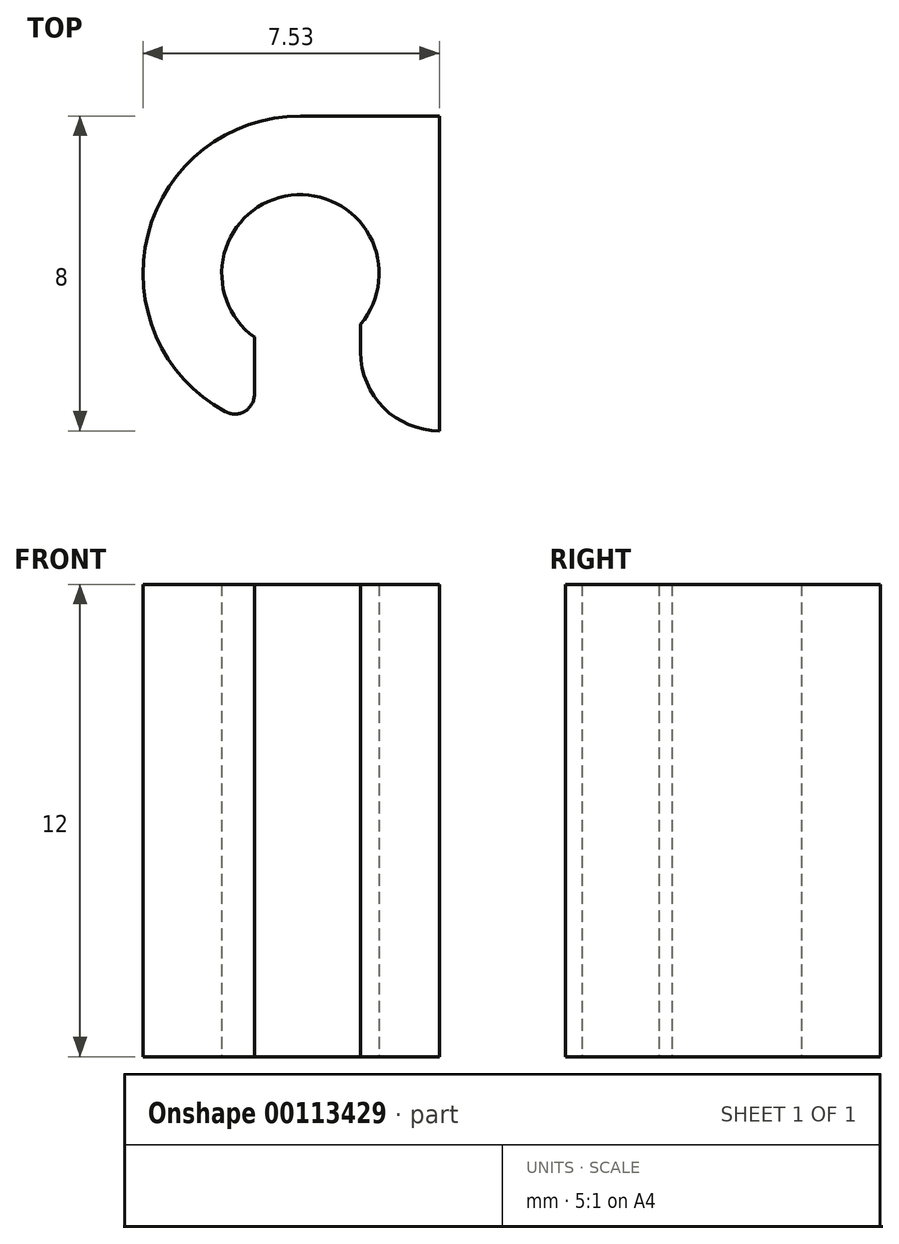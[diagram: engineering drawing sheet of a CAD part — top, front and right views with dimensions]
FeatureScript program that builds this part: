
annotation { "Feature Type Name" : "Feature", "Feature Type Description" : "" }
export const myFeature = defineFeature(function(context is Context, id is Id, definition is map)
    precondition{}
    {
        {
            var Q0;
            Q0=qCreatedBy(makeId("Top.planeOp"),FACE);
            var sketch = newSketch(context, id + "F0", { "sketchPlane" : qUnion([Q0])});
            skLineSegment(sketch, "E0.bottom", {"start": v(0, 14.36) * mm, "end": v(2, 14.36) * mm});
            skLineSegment(sketch, "E0.top", {"start": v(0, 6.36) * mm, "end": v(2, 6.36) * mm});
            skLineSegment(sketch, "E0.left", {"start": v(0, 14.36) * mm, "end": v(0, 11.65) * mm});
            skLineSegment(sketch, "E0.right", {"start": v(2, 14.36) * mm, "end": v(2, 6.36) * mm});
            skPoint(sketch, "E1.centerSnap0", {"position": v(0, 10.36) * mm});
            skLineSegment(sketch, "E2", {"start": v(-2.7, 16.04) * mm, "end": v(-2.7, 7.29) * mm, "construction": true});
            skLineSegment(sketch, "E3", {"start": v(1, 14.36) * mm, "end": v(-14.03, 14.36) * mm, "construction": true});
            skLineSegment(sketch, "E4", {"start": v(1.8, 6.36) * mm, "end": v(-14.03, 6.36) * mm, "construction": true});
            skArc(sketch, "E5", {"start": v(-1.53, 14.36) * mm, "mid": v(-5.4, 11.35) * mm, "end": v(-3.44, 6.85) * mm});
            skArc(sketch, "E6", {"start": v(0, 11.65) * mm, "mid": v(-3, 11.72) * mm, "end": v(-2.7, 8.74) * mm});
            skLineSegment(sketch, "E7", {"start": v(-2.7, 8.74) * mm, "end": v(-2.7, 7.29) * mm});
            skLineSegment(sketch, "E8", {"start": v(2.09, 14.36) * mm, "end": v(-1.53, 14.36) * mm});
            skArc(sketch, "E9.filletArc", {"start": v(-3.44, 6.85) * mm, "mid": v(-2.94, 6.86) * mm, "end": v(-2.7, 7.29) * mm});
            skArc(sketch, "E10", {"start": v(0, 9.07) * mm, "mid": v(-1.77, 12.35) * mm, "end": v(-2.7, 8.74) * mm});
            skLineSegment(sketch, "E11.trimOffspring", {"start": v(0, 9.07) * mm, "end": v(0, 6.36) * mm});
            skSolve(sketch);
        }
        {
            var Q0;
            Q0=makeQuery(id+"F0.imprint","IMPRINT",FACE,{"disambiguationData":[TD([[makeQuery(id+"F0.imprint","IMPRINT",EDGE,{"derivedFrom":sQuery(id+"F0.wireOp",EDGE,"uGqr9Zi0-OmH8-NMy4-B578-wksnZL5cZcRX")}),-1.0]])]});
            var Q1;
            {var subQ4=sQuery(id+"F0.wireOp",EDGE,"E0.bottom");Q1=makeQuery(id+"F0.imprint","IMPRINT",FACE,{"disambiguationData":[TD([[makeQuery(id+"F0.imprint","IMPRINT",EDGE,{"derivedFrom":subQ4}),-1.0]])]});}
            var Q2;
            {var subQ1=sQuery(id+"F0.wireOp",EDGE,"E5");Q2=makeQuery(id+"F0.imprint","IMPRINT",FACE,{"disambiguationData":[TD([[makeQuery(id+"F0.imprint","IMPRINT",EDGE,{"derivedFrom":subQ1}),1.0]])]});}
            var Q3;
            {var subQ2=sQuery(id+"F0.wireOp",EDGE,"E0.top");Q3=makeQuery(id+"F0.imprint","IMPRINT",FACE,{"disambiguationData":[TD([[makeQuery(id+"F0.imprint","IMPRINT",EDGE,{"derivedFrom":subQ2}),1.0]])]});}
            extrude(context, id + "F1", {"entities" : qUnion([Q0, Q1, Q2, Q3]), "depth" : 12 * mm});
        }
        {
            var Q0;
            Q0=makeQuery(id+"F1.opExtrude","SWEPT_EDGE",EDGE,{"disambiguationData":[OSD([sQuery(id+"F0.wireOp",EDGE,"E0.top"),sQuery(id+"F0.wireOp",EDGE,"E11.trimOffspring")])]});
            fillet(context, id + "F2", {"entities" : qUnion([Q0]), "radius" : 2 * mm, "tangentPropagation" : true, "allowEdgeOverflow" : false});
        }
    });
